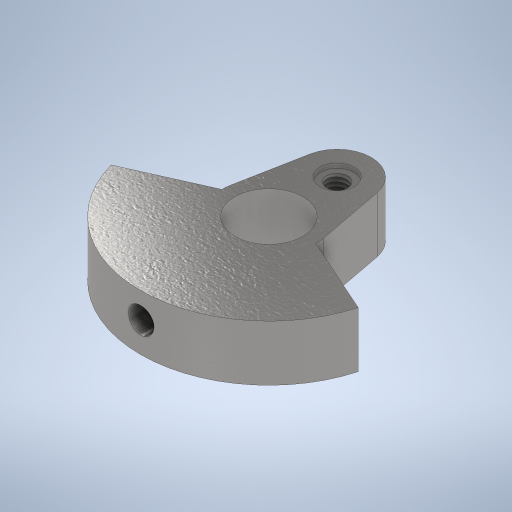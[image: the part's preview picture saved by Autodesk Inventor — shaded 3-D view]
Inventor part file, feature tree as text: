
AUTODESK INVENTOR PART (.ipt)
format: ipt  version: 2024 (Build 280153000, 153)  size: 332,800 bytes
history: native  units: mm
features: sketch x4, extrude x2, hole x2, projected_geometry x2, plane x1
ambient origin geometry x8: Origin, YZ Plane, XZ Plane, XY Plane, X Axis, Y Axis, Z Axis, Center Point
bodies: Volumenkörper1 (feature_tree)
feature tree (11):
  extrude  "Extrusion1"  Depth=11.0mm
  extrude  "Extrusion2"  Depth=4.0mm
  hole  "Bohrung1"  [1 undecoded]
  plane  "Arbeitsebene1"
  hole  "Bohrung2"  [1 undecoded]
  sketch  "Skizze1"  dims[d2=30.0mm d3=11.0mm]
  sketch  "Skizze2"  dims[d4=4.0mm d5=4.0mm]
  projected_geometry  "Projizierte Kontur1"
  sketch  "Skizze3"  dims[d6=8.0mm d7=6.5mm d8=0.0mm]
  sketch  "Skizze4"  dims[d9=8.0mm d10=0.0mm d11=0.0mm d12=8.0mm d13=2.459mm d14=6.0mm d15=4.0mm d16=0.5mm d17=90.0deg d18=9.0mm d19=20.594885mm d20=0.0mm d25=3.0mm d26=14.456832mm d27=3.0mm d28=8.0mm d29=4.0mm d30=0.5mm d31=90.0deg d32=8.0mm d33=0.0mm]
  projected_geometry  "Projizierte Kontur2"
note: 2 required parameter values undecoded (feature->parameter linkage not recoverable at this tier; creation-order binding heuristic only, values carry confidence <= 0.55)
